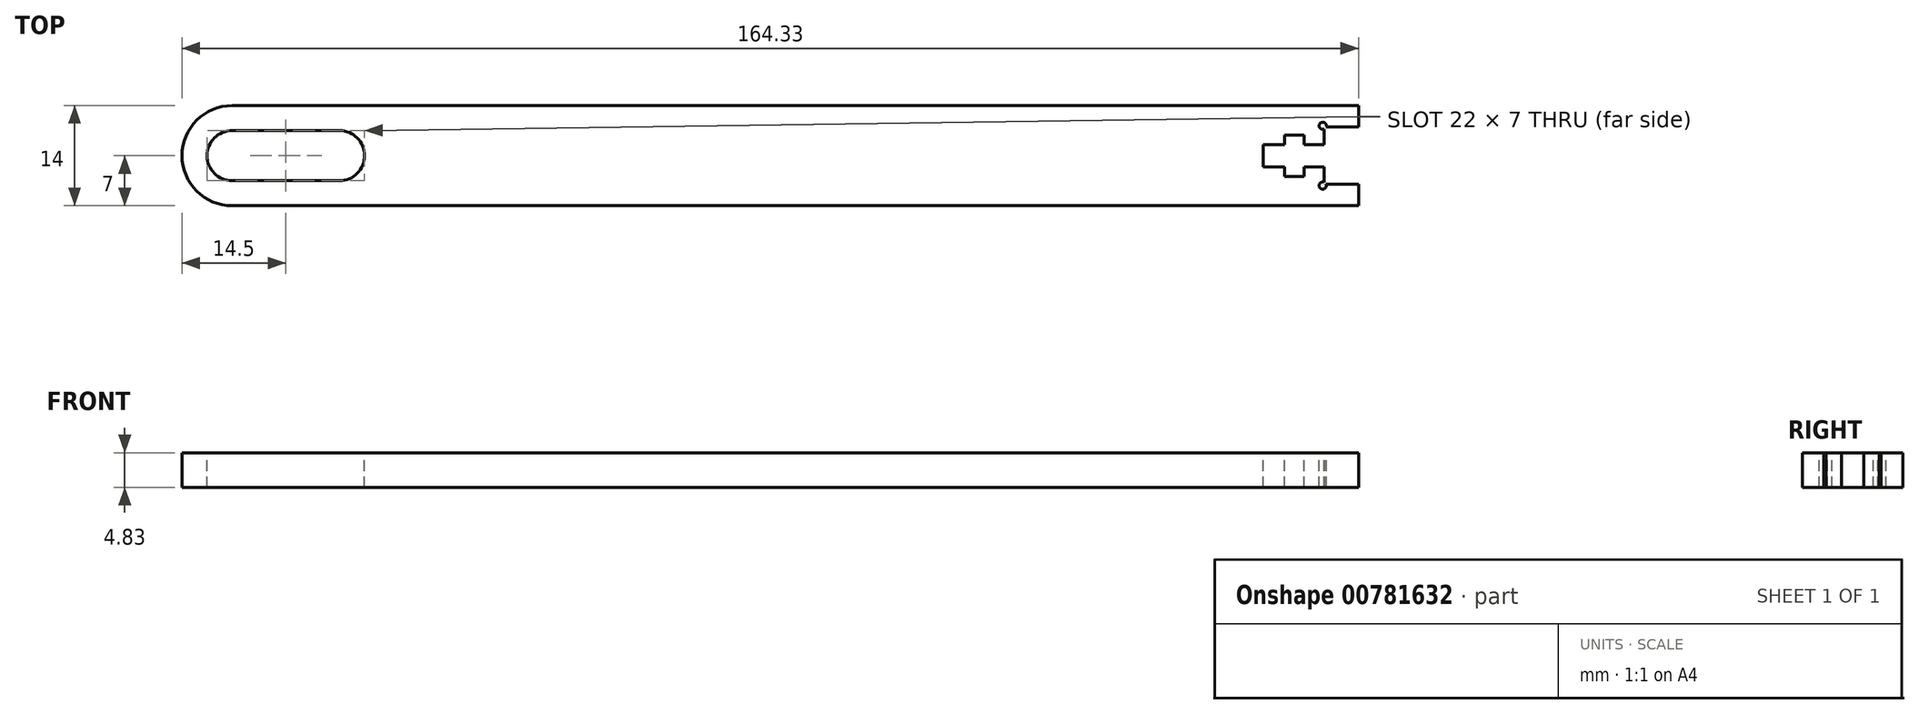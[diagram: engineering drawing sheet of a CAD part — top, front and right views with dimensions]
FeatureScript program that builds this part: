
annotation { "Feature Type Name" : "Feature", "Feature Type Description" : "" }
export const myFeature = defineFeature(function(context is Context, id is Id, definition is map)
    precondition{}
    {
        {
            var Q0;
            Q0=qCreatedBy(makeId("Top.planeOp"),FACE);
            var sketch = newSketch(context, id + "F0", { "sketchPlane" : qUnion([Q0])});
            skLineSegment(sketch, "E0.bottom", {"start": v(80, -7) * mm, "end": v(-80, -7) * mm});
            skLineSegment(sketch, "E0.top", {"start": v(80, 7) * mm, "end": v(-80, 7) * mm});
            skLineSegment(sketch, "E0.left", {"start": v(80, -7) * mm, "end": v(80, 7) * mm});
            skLineSegment(sketch, "E0.right", {"start": v(-80, -7) * mm, "end": v(-80, 7) * mm});
            skPoint(sketch, "E0.middle", {"position": v(0, 0) * mm});
            skSolve(sketch);
        }
        {
            var Q0;
            Q0 = qSketchRegion(id + "F0", true);
            extrude(context, id + "F1", {"entities" : qUnion([Q0]), "depth" : 4.83 * mm, "offsetDistance" : 25 * mm});
        }
        {
            var Q0;
            Q0=makeQuery(id+"F1.opExtrude","CAP_FACE",FACE,{"disambiguationData":[OSD([sQuery(id+"F0.wireOp",EDGE,"E0.bottom"),sQuery(id+"F0.wireOp",EDGE,"E0.top"),sQuery(id+"F0.wireOp",EDGE,"E0.left"),sQuery(id+"F0.wireOp",EDGE,"E0.right")])],"isStart":false});
            var sketch = newSketch(context, id + "F2", { "sketchPlane" : qUnion([Q0])});
            skLineSegment(sketch, "E1.bottom", {"start": v(80, 7) * mm, "end": v(84.83, 7) * mm});
            skLineSegment(sketch, "E1.top", {"start": v(80, 4) * mm, "end": v(84.83, 4) * mm});
            skLineSegment(sketch, "E1.left", {"start": v(80, 7) * mm, "end": v(80, 4) * mm});
            skLineSegment(sketch, "E1.right", {"start": v(84.83, 7) * mm, "end": v(84.83, 4) * mm});
            skLineSegment(sketch, "E2.bottom", {"start": v(80, -7) * mm, "end": v(84.83, -7) * mm});
            skLineSegment(sketch, "E2.top", {"start": v(80, -4) * mm, "end": v(84.83, -4) * mm});
            skLineSegment(sketch, "E2.left", {"start": v(80, -7) * mm, "end": v(80, -4) * mm});
            skLineSegment(sketch, "E2.right", {"start": v(84.83, -7) * mm, "end": v(84.83, -4) * mm});
            skLineSegment(sketch, "E3", {"start": v(84.83, -4) * mm, "end": v(84.83, 4) * mm, "construction": true});
            skPoint(sketch, "E4", {"position": v(84.83, 0) * mm});
            skLineSegment(sketch, "E5", {"start": v(84.83, 0) * mm, "end": v(0, 0) * mm, "construction": true});
            skLineSegment(sketch, "E6", {"start": v(71.5, -1.55) * mm, "end": v(74.5, -1.55) * mm});
            skLineSegment(sketch, "E7", {"start": v(74.5, -1.55) * mm, "end": v(74.5, -2.9) * mm});
            skLineSegment(sketch, "E8", {"start": v(74.5, -2.9) * mm, "end": v(77.2, -2.9) * mm});
            skLineSegment(sketch, "E9", {"start": v(77.2, -2.9) * mm, "end": v(77.2, -1.55) * mm});
            skLineSegment(sketch, "E10", {"start": v(77.2, -1.55) * mm, "end": v(80, -1.55) * mm});
            skLineSegment(sketch, "E11", {"start": v(80, -1.55) * mm, "end": v(80, 1.55) * mm});
            skLineSegment(sketch, "E12", {"start": v(80, 1.55) * mm, "end": v(77.2, 1.55) * mm});
            skLineSegment(sketch, "E13", {"start": v(77.2, 1.55) * mm, "end": v(77.2, 2.9) * mm});
            skLineSegment(sketch, "E14", {"start": v(77.2, 2.9) * mm, "end": v(74.5, 2.9) * mm});
            skLineSegment(sketch, "E15", {"start": v(74.5, 2.9) * mm, "end": v(74.5, 1.55) * mm});
            skLineSegment(sketch, "E16", {"start": v(74.5, 1.55) * mm, "end": v(71.5, 1.55) * mm});
            skLineSegment(sketch, "E17", {"start": v(80, 0) * mm, "end": v(71.5, 0) * mm, "construction": true});
            skLineSegment(sketch, "E18", {"start": v(71.5, -1.55) * mm, "end": v(71.5, 1.55) * mm});
            skPoint(sketch, "E19", {"position": v(80, 0) * mm});
            skSolve(sketch);
        }
        {
            var Q0;
            Q0=makeQuery(id+"F2.imprint","IMPRINT",FACE,{"disambiguationData":[TD([[makeQuery(id+"F2.imprint","IMPRINT",EDGE,{"derivedFrom":sQuery(id+"F2.wireOp",EDGE,"E1.bottom")}),-1.0]])]});
            var Q1;
            Q1=makeQuery(id+"F2.imprint","IMPRINT",FACE,{"disambiguationData":[TD([[makeQuery(id+"F2.imprint","IMPRINT",EDGE,{"derivedFrom":sQuery(id+"F2.wireOp",EDGE,"E2.bottom")}),1.0]])]});
            var Q2;
            Q2=makeQuery(id+"F1.opExtrude","CAP_FACE",FACE,{"disambiguationData":[OSD([sQuery(id+"F0.wireOp",EDGE,"E0.bottom"),sQuery(id+"F0.wireOp",EDGE,"E0.top"),sQuery(id+"F0.wireOp",EDGE,"E0.left"),sQuery(id+"F0.wireOp",EDGE,"E0.right")])],"isStart":true});
            extrude(context, id + "F3", {"entities" : qUnion([Q0, Q1]), "operationType" : NewBodyOperationType.ADD, "endBound" : BoundingType.UP_TO_SURFACE, "oppositeDirection" : true, "depth" : 25 * mm, "endBoundEntityFace" : qUnion([Q2]), "offsetDistance" : 25 * mm});
        }
        {
            var Q0;
            Q0=makeQuery(id+"F2.imprint","IMPRINT",FACE,{"disambiguationData":[TD([[makeQuery(id+"F2.imprint","IMPRINT",EDGE,{"derivedFrom":sQuery(id+"F2.wireOp",EDGE,"E6")}),1.0]])]});
            extrude(context, id + "F4", {"entities" : qUnion([Q0]), "operationType" : NewBodyOperationType.REMOVE, "oppositeDirection" : true, "depth" : 25 * mm, "offsetDistance" : 25 * mm});
        }
        {
            var Q0;
            Q0=makeQuery(id+"F3.boolean.opBoolean","MERGE",FACE,{"derivedFrom":[makeQuery(id+"F1.opExtrude","CAP_FACE",FACE,{"disambiguationData":[OSD([sQuery(id+"F0.wireOp",EDGE,"E0.bottom"),sQuery(id+"F0.wireOp",EDGE,"E0.top"),sQuery(id+"F0.wireOp",EDGE,"E0.left"),sQuery(id+"F0.wireOp",EDGE,"E0.right")])],"isStart":false}),makeQuery(id+"F3.opExtrude","CAP_FACE",FACE,{"disambiguationData":[OSD([sQuery(id+"F2.wireOp",EDGE,"E1.bottom"),sQuery(id+"F2.wireOp",EDGE,"E1.top"),sQuery(id+"F2.wireOp",EDGE,"E1.left"),sQuery(id+"F2.wireOp",EDGE,"E1.right")])],"isStart":true}),makeQuery(id+"F3.opExtrude","CAP_FACE",FACE,{"disambiguationData":[OSD([sQuery(id+"F2.wireOp",EDGE,"E2.bottom"),sQuery(id+"F2.wireOp",EDGE,"E2.top"),sQuery(id+"F2.wireOp",EDGE,"E2.left"),sQuery(id+"F2.wireOp",EDGE,"E2.right")])],"isStart":true})]});
            var sketch = newSketch(context, id + "F5", { "sketchPlane" : qUnion([Q0])});
            skLineSegment(sketch, "E20", {"start": v(80, 4) * mm, "end": v(79.82, 4.18) * mm, "construction": true});
            skLineSegment(sketch, "E21", {"start": v(0, 0) * mm, "end": v(71.5, 0) * mm, "construction": true});
            skCircle(sketch, "E22", {"center": v(79.82, 4.18) * mm, "radius": 0.5 * mm});
            skCircle(sketch, "E23.MirrorC", {"center": v(79.82, -4.18) * mm, "radius": 0.5 * mm});
            skSolve(sketch);
        }
        {
            var Q0;
            Q0 = qSketchRegion(id + "F5", true);
            extrude(context, id + "F6", {"entities" : qUnion([Q0]), "operationType" : NewBodyOperationType.REMOVE, "endBound" : BoundingType.THROUGH_ALL, "oppositeDirection" : true, "depth" : 25 * mm, "offsetDistance" : 25 * mm});
        }
        {
            var Q0;
            Q0=makeQuery(id+"F3.boolean.opBoolean","MERGE",FACE,{"derivedFrom":[makeQuery(id+"F1.opExtrude","CAP_FACE",FACE,{"disambiguationData":[OSD([sQuery(id+"F0.wireOp",EDGE,"E0.bottom"),sQuery(id+"F0.wireOp",EDGE,"E0.top"),sQuery(id+"F0.wireOp",EDGE,"E0.left"),sQuery(id+"F0.wireOp",EDGE,"E0.right")])],"isStart":false}),makeQuery(id+"F3.opExtrude","CAP_FACE",FACE,{"disambiguationData":[OSD([sQuery(id+"F2.wireOp",EDGE,"E1.bottom"),sQuery(id+"F2.wireOp",EDGE,"E1.top"),sQuery(id+"F2.wireOp",EDGE,"E1.left"),sQuery(id+"F2.wireOp",EDGE,"E1.right")])],"isStart":true}),makeQuery(id+"F3.opExtrude","CAP_FACE",FACE,{"disambiguationData":[OSD([sQuery(id+"F2.wireOp",EDGE,"E2.bottom"),sQuery(id+"F2.wireOp",EDGE,"E2.top"),sQuery(id+"F2.wireOp",EDGE,"E2.left"),sQuery(id+"F2.wireOp",EDGE,"E2.right")])],"isStart":true})]});
            var sketch = newSketch(context, id + "F7", { "sketchPlane" : qUnion([Q0])});
            skArc(sketch, "E24", {"start": v(-72.5, 3.5) * mm, "mid": v(-76, 0) * mm, "end": v(-72.5, -3.5) * mm});
            skArc(sketch, "E25", {"start": v(-57.5, -3.5) * mm, "mid": v(-54, 0) * mm, "end": v(-57.5, 3.5) * mm});
            skLineSegment(sketch, "E26", {"start": v(-72.5, 3.5) * mm, "end": v(-57.5, 3.5) * mm});
            skLineSegment(sketch, "E27", {"start": v(-72.5, -3.5) * mm, "end": v(-57.5, -3.5) * mm});
            skLineSegment(sketch, "E28", {"start": v(-72.5, 0) * mm, "end": v(-57.5, 0) * mm, "construction": true});
            skPoint(sketch, "E29", {"position": v(-65, 0) * mm});
            skSolve(sketch);
        }
        {
            var Q0;
            Q0 = qSketchRegion(id + "F7", true);
            extrude(context, id + "F8", {"entities" : qUnion([Q0]), "operationType" : NewBodyOperationType.REMOVE, "endBound" : BoundingType.THROUGH_ALL, "oppositeDirection" : true, "depth" : 25 * mm, "offsetDistance" : 25 * mm});
        }
        {
            var Q0;
            Q0=makeQuery(id+"F3.boolean.opBoolean","MERGE",FACE,{"derivedFrom":[makeQuery(id+"F1.opExtrude","CAP_FACE",FACE,{"disambiguationData":[OSD([sQuery(id+"F0.wireOp",EDGE,"E0.bottom"),sQuery(id+"F0.wireOp",EDGE,"E0.top"),sQuery(id+"F0.wireOp",EDGE,"E0.left"),sQuery(id+"F0.wireOp",EDGE,"E0.right")])],"isStart":false}),makeQuery(id+"F3.opExtrude","CAP_FACE",FACE,{"disambiguationData":[OSD([sQuery(id+"F2.wireOp",EDGE,"E1.bottom"),sQuery(id+"F2.wireOp",EDGE,"E1.top"),sQuery(id+"F2.wireOp",EDGE,"E1.left"),sQuery(id+"F2.wireOp",EDGE,"E1.right")])],"isStart":true}),makeQuery(id+"F3.opExtrude","CAP_FACE",FACE,{"disambiguationData":[OSD([sQuery(id+"F2.wireOp",EDGE,"E2.bottom"),sQuery(id+"F2.wireOp",EDGE,"E2.top"),sQuery(id+"F2.wireOp",EDGE,"E2.left"),sQuery(id+"F2.wireOp",EDGE,"E2.right")])],"isStart":true})]});
            var sketch = newSketch(context, id + "F9", { "sketchPlane" : qUnion([Q0])});
            skArc(sketch, "E30", {"start": v(-72.5, 7) * mm, "mid": v(-79.5, 0) * mm, "end": v(-72.5, -7) * mm});
            skLineSegment(sketch, "E31", {"start": v(-72.5, 7) * mm, "end": v(-80, 7) * mm});
            skLineSegment(sketch, "E32", {"start": v(-80, 7) * mm, "end": v(-80, -7) * mm});
            skLineSegment(sketch, "E33", {"start": v(-80, -7) * mm, "end": v(-72.1, -7) * mm});
            skSolve(sketch);
        }
        {
            var Q0;
            Q0 = qSketchRegion(id + "F9", true);
            extrude(context, id + "F10", {"entities" : qUnion([Q0]), "operationType" : NewBodyOperationType.REMOVE, "endBound" : BoundingType.THROUGH_ALL, "oppositeDirection" : true, "depth" : 25 * mm, "offsetDistance" : 25 * mm});
        }
    });
